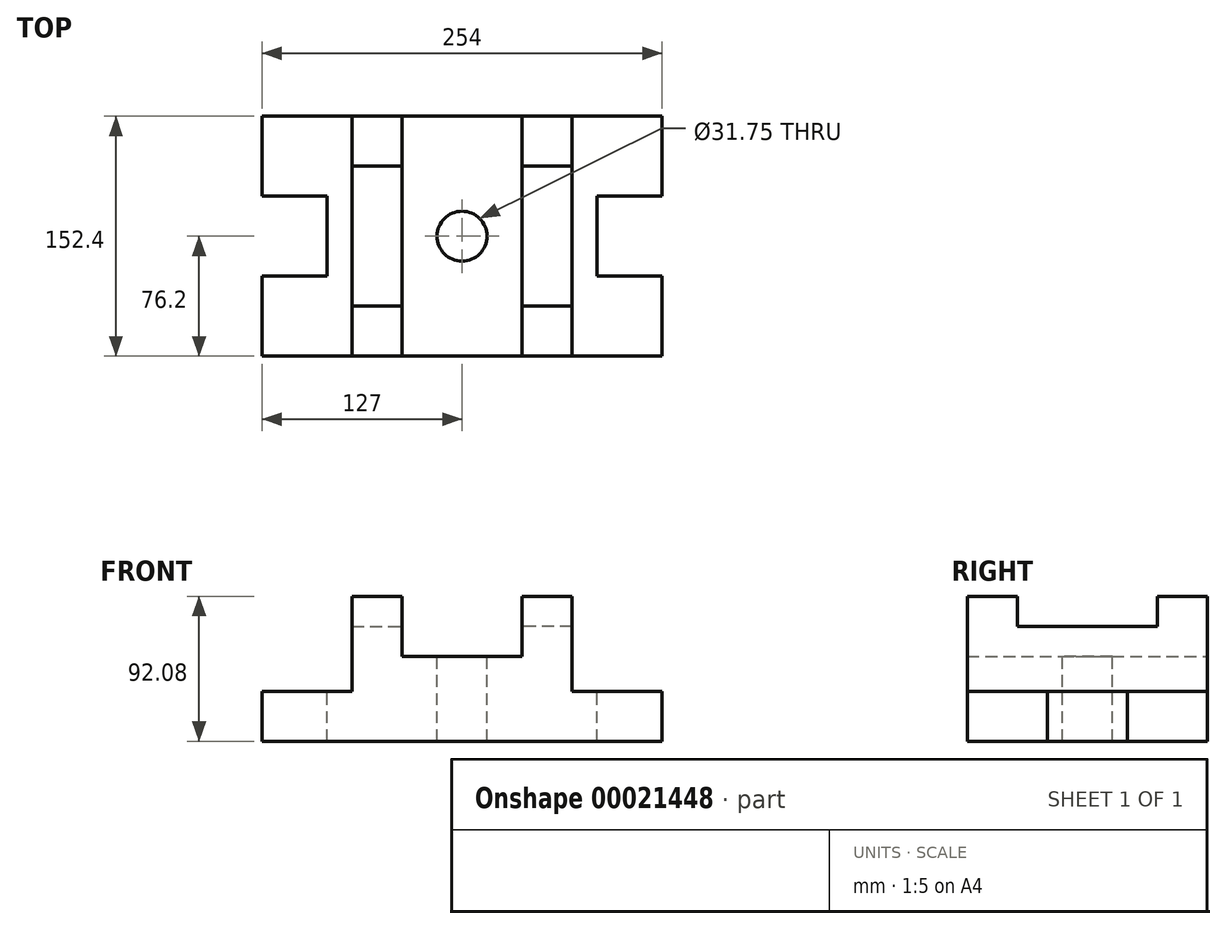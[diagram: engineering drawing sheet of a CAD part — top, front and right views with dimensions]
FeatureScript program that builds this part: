
annotation { "Feature Type Name" : "Feature", "Feature Type Description" : "" }
export const myFeature = defineFeature(function(context is Context, id is Id, definition is map)
    precondition{}
    {
        {
            var Q0;
            Q0=qCreatedBy(makeId("Front.planeOp"),FACE);
            var sketch = newSketch(context, id + "F0", { "sketchPlane" : qUnion([Q0])});
            skLineSegment(sketch, "E0.rect.bottom", {"start": v(-63.5, 46.04) * mm, "end": v(63.5, 46.04) * mm});
            skLineSegment(sketch, "E0.rect.top", {"start": v(-63.5, -46.04) * mm, "end": v(63.5, -46.04) * mm});
            skLineSegment(sketch, "E0.rect.left", {"start": v(-63.5, 46.04) * mm, "end": v(-63.5, -46.04) * mm});
            skLineSegment(sketch, "E0.rect.right", {"start": v(63.5, 46.04) * mm, "end": v(63.5, -46.04) * mm});
            skPoint(sketch, "E0.rect.middle", {"position": v(0, 0) * mm});
            skLineSegment(sketch, "E1", {"start": v(-63.5, 7.94) * mm, "end": v(-25.4, 7.94) * mm});
            skLineSegment(sketch, "E2", {"start": v(-25.4, 7.94) * mm, "end": v(-25.4, 46.04) * mm});
            skLineSegment(sketch, "E3.bottom", {"start": v(63.5, 46.04) * mm, "end": v(6.35, 46.04) * mm});
            skLineSegment(sketch, "E3.top", {"start": v(63.5, -14.29) * mm, "end": v(6.35, -14.29) * mm});
            skLineSegment(sketch, "E3.left", {"start": v(63.5, 46.04) * mm, "end": v(63.5, -14.29) * mm});
            skLineSegment(sketch, "E3.right", {"start": v(6.35, 46.04) * mm, "end": v(6.35, -14.29) * mm});
            skSolve(sketch);
        }
        {
            var Q0;
            {var subQ4=sQuery(id+"F0.wireOp",EDGE,"E0.rect.top");Q0=makeQuery(id+"F0.imprint","IMPRINT",FACE,{"disambiguationData":[TD([[makeQuery(id+"F0.imprint","IMPRINT",EDGE,{"derivedFrom":subQ4}),1.0]])]});}
            extrude(context, id + "F1", {"entities" : qUnion([Q0]), "depth" : 76.2 * mm});
        }
        {
            var Q0;
            Q0=makeQuery(id+"F1.opExtrude","CAP_FACE",FACE,{"disambiguationData":[OSD([sQuery(id+"F0.wireOp",EDGE,"E0.rect.bottom"),sQuery(id+"F0.wireOp",EDGE,"E0.rect.top"),sQuery(id+"F0.wireOp",EDGE,"E0.rect.left"),sQuery(id+"F0.wireOp",EDGE,"E0.rect.right"),sQuery(id+"F0.wireOp",EDGE,"E1"),sQuery(id+"F0.wireOp",EDGE,"E2"),sQuery(id+"F0.wireOp",EDGE,"E3.top"),sQuery(id+"F0.wireOp",EDGE,"E3.right")])],"isStart":true});
            var sketch = newSketch(context, id + "F2", { "sketchPlane" : qUnion([Q0])});
            skLineSegment(sketch, "E4", {"start": v(-6.35, 26.99) * mm, "end": v(25.4, 26.99) * mm});
            skLineSegment(sketch, "E5", {"start": v(-6.35, 26.99) * mm, "end": v(-6.35, 46.04) * mm});
            skLineSegment(sketch, "E6", {"start": v(-6.35, 46.04) * mm, "end": v(25.4, 46.04) * mm});
            skLineSegment(sketch, "E7", {"start": v(25.4, 46.04) * mm, "end": v(25.4, 26.99) * mm});
            skSolve(sketch);
        }
        {
            var Q0;
            Q0=makeQuery(id+"F2.imprint","IMPRINT",FACE,{"disambiguationData":[TD([[makeQuery(id+"F2.imprint","IMPRINT",EDGE,{"derivedFrom":sQuery(id+"F2.wireOp",EDGE,"E4")}),1.0]])]});
            extrude(context, id + "F3", {"entities" : qUnion([Q0]), "operationType" : NewBodyOperationType.REMOVE, "oppositeDirection" : true, "depth" : 44.45 * mm});
        }
        {
            var Q0;
            Q0=makeQuery(id+"F1.opExtrude","SWEPT_FACE",FACE,{"disambiguationData":[OSD([sQuery(id+"F0.wireOp",EDGE,"E3.top")])]});
            var sketch = newSketch(context, id + "F4", { "sketchPlane" : qUnion([Q0])});
            skLineSegment(sketch, "E8", {"start": v(63.5, -25.4) * mm, "end": v(22.23, -25.4) * mm});
            skLineSegment(sketch, "E9", {"start": v(22.23, -25.4) * mm, "end": v(22.23, 0) * mm});
            skLineSegment(sketch, "E10", {"start": v(22.23, 0) * mm, "end": v(63.5, 0) * mm});
            skLineSegment(sketch, "E11", {"start": v(63.5, 0) * mm, "end": v(63.5, -25.4) * mm});
            skSolve(sketch);
        }
        {
            var Q0;
            Q0=makeQuery(id+"F4.imprint","IMPRINT",FACE,{"disambiguationData":[TD([[makeQuery(id+"F4.imprint","IMPRINT",EDGE,{"derivedFrom":sQuery(id+"F4.wireOp",EDGE,"E8")}),-1.0]])]});
            extrude(context, id + "F5", {"entities" : qUnion([Q0]), "operationType" : NewBodyOperationType.REMOVE, "oppositeDirection" : true, "depth" : 31.75 * mm});
        }
        {
            var Q0;
            Q0=makeQuery(id+"F1.opExtrude","SWEPT_FACE",FACE,{"disambiguationData":[OSD([sQuery(id+"F0.wireOp",EDGE,"E1")])]});
            var sketch = newSketch(context, id + "F6", { "sketchPlane" : qUnion([Q0])});
            skCircle(sketch, "E12", {"center": v(-63.5, 0) * mm, "radius": 15.88 * mm});
            skSolve(sketch);
        }
        {
            var Q0;
            {var subQ0=sQuery(id+"F0.wireOp",EDGE,"E1");var subQ1=makeQuery(id+"F1.opExtrude","CAP_EDGE",EDGE,{"disambiguationData":[OSD([subQ0])],"isStart":true});var subQ2=sQuery(id+"F6.wireOp",EDGE,"E12");var subQ3=makeQuery(id+"F6.imprint","INTERSECT",VERTEX,{"derivedFrom":[subQ1,subQ2]});Q0=makeQuery(id+"F6.imprint","IMPRINT",FACE,{"disambiguationData":[TD([[makeQuery(id+"F6.imprint","IMPRINT",EDGE,{"disambiguationData":[TD([[subQ3,1.0]])],"derivedFrom":subQ2}),1.0]])]});}
            extrude(context, id + "F7", {"entities" : qUnion([Q0]), "operationType" : NewBodyOperationType.REMOVE, "oppositeDirection" : true, "depth" : 53.97 * mm});
        }
        {
            var Q0;
            Q0=makeQuery(id+"F1.opExtrude","SWEPT_BODY",BODY,{"disambiguationData":[OSD([sQuery(id+"F0.wireOp",EDGE,"E0.rect.bottom"),sQuery(id+"F0.wireOp",EDGE,"E0.rect.top"),sQuery(id+"F0.wireOp",EDGE,"E0.rect.left"),sQuery(id+"F0.wireOp",EDGE,"E0.rect.right"),sQuery(id+"F0.wireOp",EDGE,"E1"),sQuery(id+"F0.wireOp",EDGE,"E2"),sQuery(id+"F0.wireOp",EDGE,"E3.top"),sQuery(id+"F0.wireOp",EDGE,"E3.right")])]});
            var Q1;
            Q1=makeQuery(id+"F1.opExtrude","CAP_FACE",FACE,{"disambiguationData":[OSD([sQuery(id+"F0.wireOp",EDGE,"E0.rect.bottom"),sQuery(id+"F0.wireOp",EDGE,"E0.rect.top"),sQuery(id+"F0.wireOp",EDGE,"E0.rect.left"),sQuery(id+"F0.wireOp",EDGE,"E0.rect.right"),sQuery(id+"F0.wireOp",EDGE,"E1"),sQuery(id+"F0.wireOp",EDGE,"E2"),sQuery(id+"F0.wireOp",EDGE,"E3.top"),sQuery(id+"F0.wireOp",EDGE,"E3.right")])],"isStart":true});
            mirror(context, id + "F8", {"operationType" : NewBodyOperationType.ADD, "entities" : qUnion([Q0]), "mirrorPlane" : qUnion([Q1])});
        }
        {
            var Q0;
            Q0=makeQuery(id+"F1.opExtrude","SWEPT_BODY",BODY,{"disambiguationData":[OSD([sQuery(id+"F0.wireOp",EDGE,"E0.rect.bottom"),sQuery(id+"F0.wireOp",EDGE,"E0.rect.top"),sQuery(id+"F0.wireOp",EDGE,"E0.rect.left"),sQuery(id+"F0.wireOp",EDGE,"E0.rect.right"),sQuery(id+"F0.wireOp",EDGE,"E1"),sQuery(id+"F0.wireOp",EDGE,"E2"),sQuery(id+"F0.wireOp",EDGE,"E3.top"),sQuery(id+"F0.wireOp",EDGE,"E3.right")])]});
            var Q1;
            Q1=makeQuery(id+"F8.opPattern","COPY",FACE,{"derivedFrom":makeQuery(id+"F1.opExtrude","SWEPT_FACE",FACE,{"disambiguationData":[OSD([sQuery(id+"F0.wireOp",EDGE,"E0.rect.left")])]}),"instanceName":"1"});
            mirror(context, id + "F9", {"operationType" : NewBodyOperationType.ADD, "entities" : qUnion([Q0]), "mirrorPlane" : qUnion([Q1])});
        }
    });
